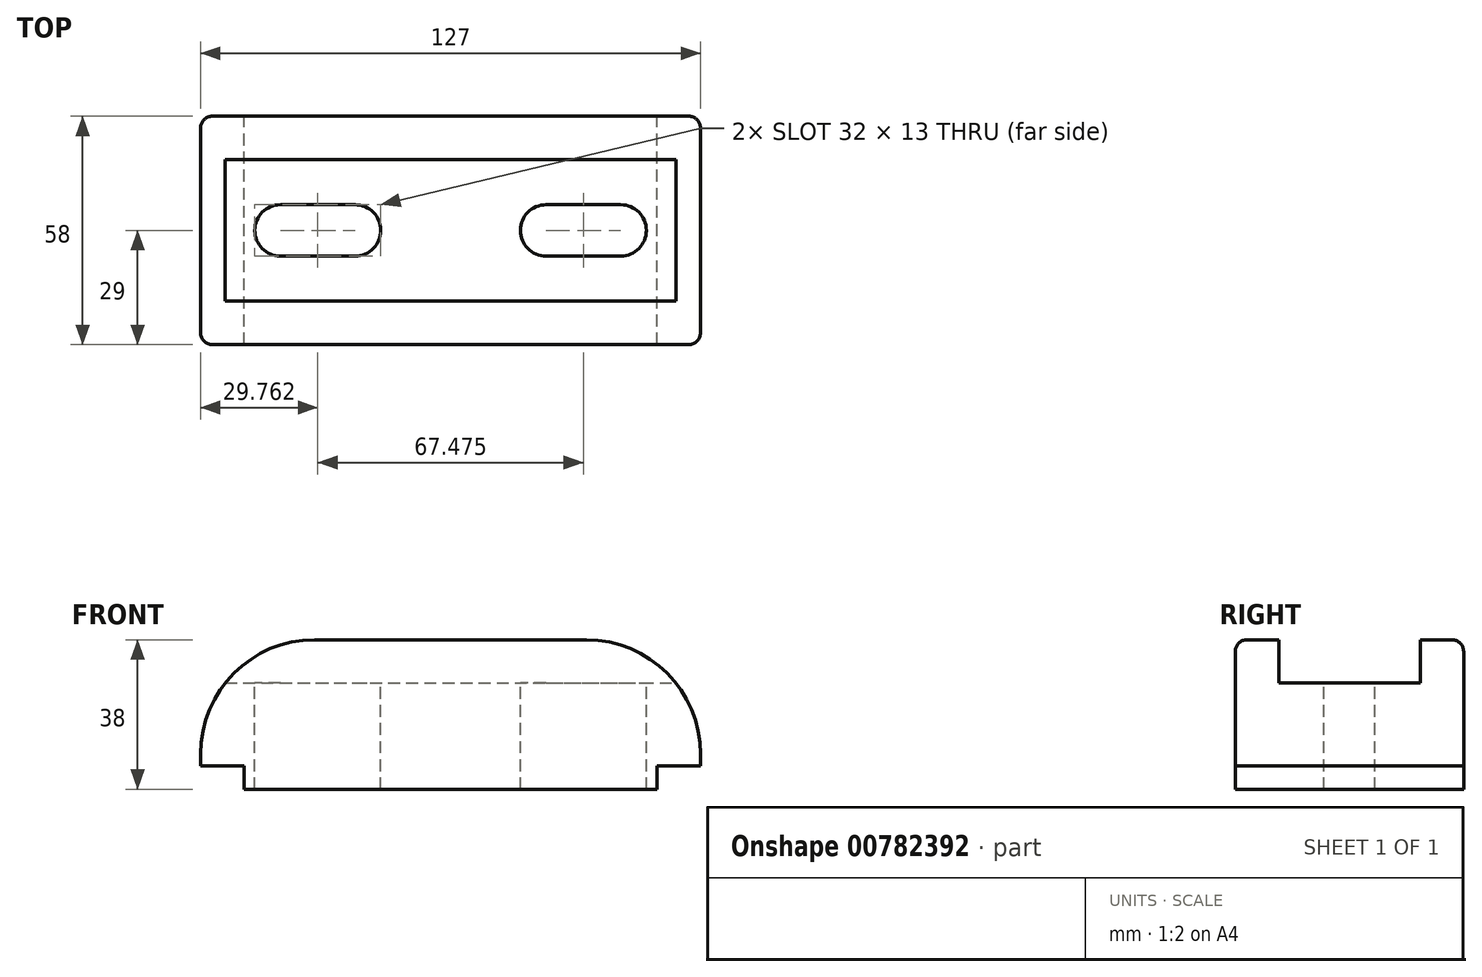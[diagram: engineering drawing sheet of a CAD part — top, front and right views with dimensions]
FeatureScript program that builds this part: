
annotation { "Feature Type Name" : "Feature", "Feature Type Description" : "" }
export const myFeature = defineFeature(function(context is Context, id is Id, definition is map)
    precondition{}
    {
        {
            var Q0;
            Q0=qCreatedBy(makeId("Front.planeOp"),FACE);
            var sketch = newSketch(context, id + "F0", { "sketchPlane" : qUnion([Q0])});
            skLineSegment(sketch, "E0.bottom", {"start": v(-34.5, 19) * mm, "end": v(34.5, 19) * mm});
            skLineSegment(sketch, "E0.top", {"start": v(-52.5, -19) * mm, "end": v(52.5, -19) * mm});
            skLineSegment(sketch, "E0.left", {"start": v(-63.5, -10) * mm, "end": v(-63.5, -13) * mm});
            skLineSegment(sketch, "E0.right", {"start": v(63.5, -10) * mm, "end": v(63.5, -13) * mm});
            skPoint(sketch, "E0.middle", {"position": v(0, 0) * mm});
            skPoint(sketch, "E1.visualSharp", {"position": v(-63.5, 19) * mm});
            skArc(sketch, "E1.filletArc", {"start": v(-34.5, 19) * mm, "mid": v(-55, 10.5) * mm, "end": v(-63.5, -10) * mm});
            skPoint(sketch, "E2.visualSharp", {"position": v(63.5, 19) * mm});
            skArc(sketch, "E2.filletArc", {"start": v(63.5, -10) * mm, "mid": v(55, 10.5) * mm, "end": v(34.5, 19) * mm});
            skLineSegment(sketch, "E3.top", {"start": v(-63.5, -13) * mm, "end": v(-52.5, -13) * mm});
            skLineSegment(sketch, "E3.right", {"start": v(-52.5, -19) * mm, "end": v(-52.5, -13) * mm});
            skLineSegment(sketch, "E4.top", {"start": v(63.5, -13) * mm, "end": v(52.5, -13) * mm});
            skLineSegment(sketch, "E4.right", {"start": v(52.5, -19) * mm, "end": v(52.5, -13) * mm});
            skPoint(sketch, "E5.orphan", {"position": v(63.5, -19) * mm});
            skPoint(sketch, "E6.orphan", {"position": v(-63.5, -19) * mm});
            skSolve(sketch);
        }
        {
            var Q0;
            Q0 = qSketchRegion(id + "F0", true);
            extrude(context, id + "F1", {"entities" : qUnion([Q0]), "endBound" : BoundingType.SYMMETRIC, "depth" : 58 * mm, "offsetDistance" : 25.4 * mm});
        }
        {
            var Q0;
            Q0=makeQuery(id+"F1.opExtrude","SWEPT_FACE",FACE,{"disambiguationData":[OSD([sQuery(id+"F0.wireOp",EDGE,"E0.bottom")])]});
            var sketch = newSketch(context, id + "F2", { "sketchPlane" : qUnion([Q0])});
            skLineSegment(sketch, "E7.bottom", {"start": v(-83.27, -18) * mm, "end": v(71.92, -18) * mm});
            skLineSegment(sketch, "E7.top", {"start": v(-83.27, 18) * mm, "end": v(71.92, 18) * mm});
            skLineSegment(sketch, "E7.left", {"start": v(-83.27, -18) * mm, "end": v(-83.27, 18) * mm});
            skLineSegment(sketch, "E7.right", {"start": v(71.92, -18) * mm, "end": v(71.92, 18) * mm});
            skSolve(sketch);
        }
        {
            var Q0;
            Q0 = qSketchRegion(id + "F2", true);
            extrude(context, id + "F3", {"entities" : qUnion([Q0]), "operationType" : NewBodyOperationType.REMOVE, "oppositeDirection" : true, "depth" : 11 * mm, "offsetDistance" : 25.4 * mm});
        }
        {
            var Q0;
            Q0=makeQuery(id+"F3.boolean.opBoolean","COPY",FACE,{"derivedFrom":makeQuery(id+"F3.opExtrude","CAP_FACE",FACE,{"disambiguationData":[OSD([sQuery(id+"F2.wireOp",EDGE,"E7.bottom"),sQuery(id+"F2.wireOp",EDGE,"E7.top"),sQuery(id+"F2.wireOp",EDGE,"E7.left"),sQuery(id+"F2.wireOp",EDGE,"E7.right")])],"isStart":false})});
            var sketch = newSketch(context, id + "F4", { "sketchPlane" : qUnion([Q0])});
            skLineSegment(sketch, "E8", {"start": v(-43.24, 6.5) * mm, "end": v(-24.24, 6.5) * mm});
            skLineSegment(sketch, "E9", {"start": v(-24.24, -6.5) * mm, "end": v(-43.24, -6.5) * mm});
            skLineSegment(sketch, "E10", {"start": v(24.24, 6.5) * mm, "end": v(43.24, 6.5) * mm});
            skLineSegment(sketch, "E11", {"start": v(24.24, -6.5) * mm, "end": v(43.24, -6.5) * mm});
            skArc(sketch, "E12", {"start": v(-43.24, 6.5) * mm, "mid": v(-49.74, 0) * mm, "end": v(-43.24, -6.5) * mm});
            skArc(sketch, "E13", {"start": v(-24.24, -6.5) * mm, "mid": v(-17.74, 0) * mm, "end": v(-24.24, 6.5) * mm});
            skArc(sketch, "E14", {"start": v(24.24, 6.5) * mm, "mid": v(17.74, 0) * mm, "end": v(24.24, -6.5) * mm});
            skArc(sketch, "E15", {"start": v(43.24, -6.5) * mm, "mid": v(49.74, 0) * mm, "end": v(43.24, 6.5) * mm});
            skSolve(sketch);
        }
        {
            var Q0;
            Q0 = qSketchRegion(id + "F4", true);
            extrude(context, id + "F5", {"entities" : qUnion([Q0]), "operationType" : NewBodyOperationType.REMOVE, "endBound" : BoundingType.THROUGH_ALL, "oppositeDirection" : true, "depth" : 25.4 * mm, "offsetDistance" : 25.4 * mm});
        }
        {
            var Q0;
            Q0=makeQuery(id+"F1.opExtrude","CAP_EDGE",EDGE,{"disambiguationData":[OSD([sQuery(id+"F0.wireOp",EDGE,"E1.filletArc")])],"isStart":false});
            var Q1;
            Q1=makeQuery(id+"F1.opExtrude","CAP_EDGE",EDGE,{"disambiguationData":[OSD([sQuery(id+"F0.wireOp",EDGE,"E2.filletArc")])],"isStart":true});
            fillet(context, id + "F6", {"entities" : qUnion([Q0, Q1]), "radius" : 3 * mm, "tangentPropagation" : true, "allowEdgeOverflow" : false});
        }
    });
